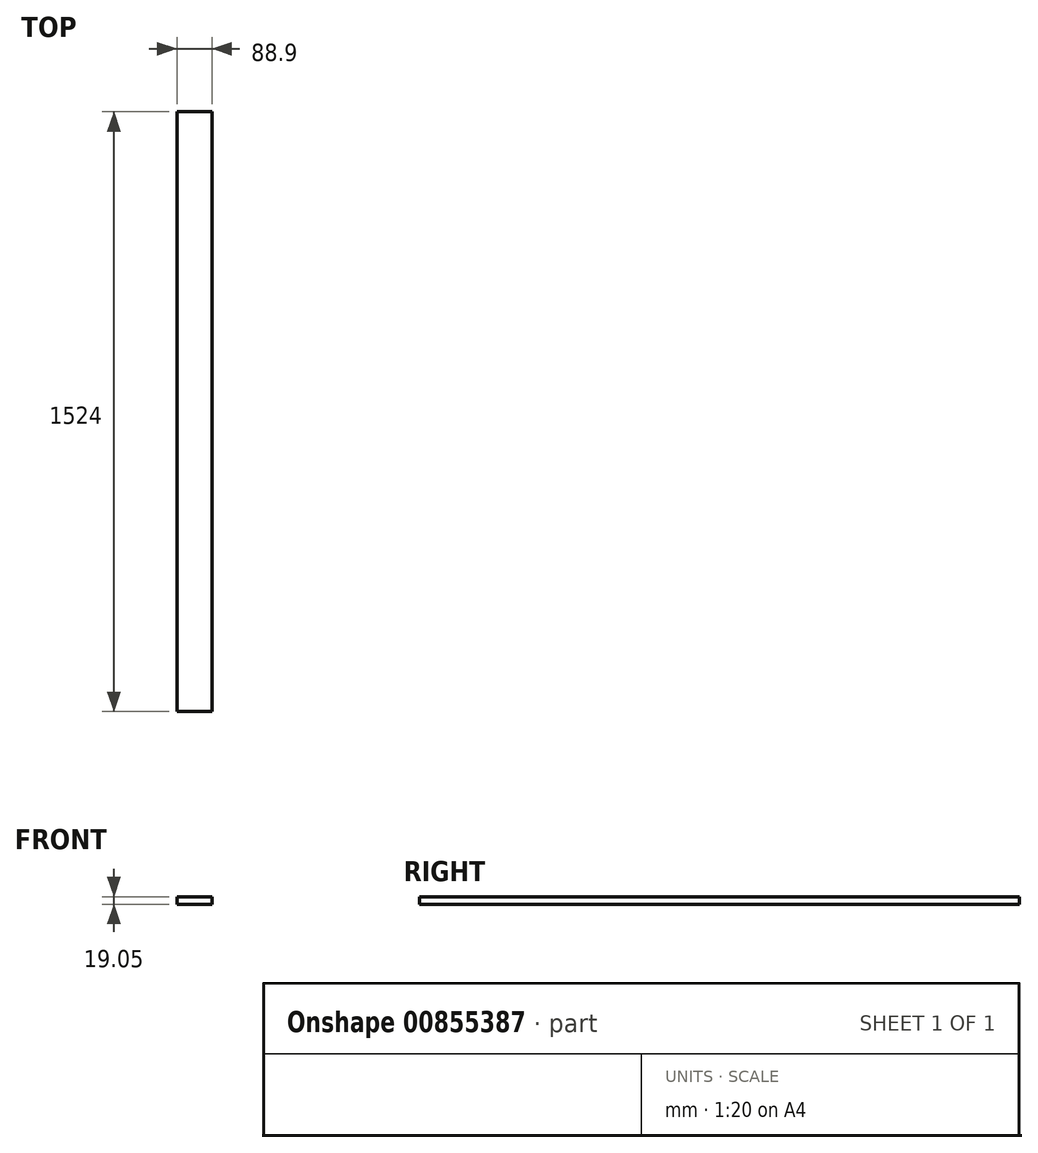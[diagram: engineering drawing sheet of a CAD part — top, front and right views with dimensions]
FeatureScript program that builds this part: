
annotation { "Feature Type Name" : "Feature", "Feature Type Description" : "" }
export const myFeature = defineFeature(function(context is Context, id is Id, definition is map)
    precondition{}
    {
        {
            var Q0;
            Q0=qCreatedBy(makeId("Front.planeOp"),FACE);
            var sketch = newSketch(context, id + "F0", { "sketchPlane" : qUnion([Q0])});
            skLineSegment(sketch, "E0.bottom", {"start": v(0, 0) * mm, "end": v(88.9, 0) * mm});
            skLineSegment(sketch, "E0.top", {"start": v(0, 19.05) * mm, "end": v(88.9, 19.05) * mm});
            skLineSegment(sketch, "E0.left", {"start": v(0, 0) * mm, "end": v(0, 19.05) * mm});
            skLineSegment(sketch, "E0.right", {"start": v(88.9, 0) * mm, "end": v(88.9, 19.05) * mm});
            skSolve(sketch);
        }
        {
            var Q0;
            Q0 = qSketchRegion(id + "F0", true);
            extrude(context, id + "F1", {"entities" : qUnion([Q0]), "depth" : 1524 * mm, "offsetDistance" : 25.4 * mm});
        }
    });
